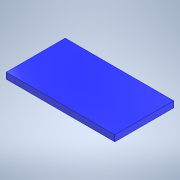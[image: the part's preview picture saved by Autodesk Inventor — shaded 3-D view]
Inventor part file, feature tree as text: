
AUTODESK INVENTOR PART (.ipt)
format: ipt  version: 2022 (Build 260153000, 153)  size: 94,208 bytes
history: native  units: in
note: dims shown in document units (in); Inventor stores cm internally (conversion verified against a paired STEP export)
features: extrude x1, sketch x1
ambient origin geometry x8: Origin, YZ Plane, XZ Plane, XY Plane, X Axis, Y Axis, Z Axis, Center Point
bodies: Solid1 (feature_tree)
feature tree (2):
  extrude  "Extrusion1"  Depth=1.45in
  sketch  "Sketch1"  dims[d0=2.67in d1=1.45in d2=0.15in d3=0.0in]
